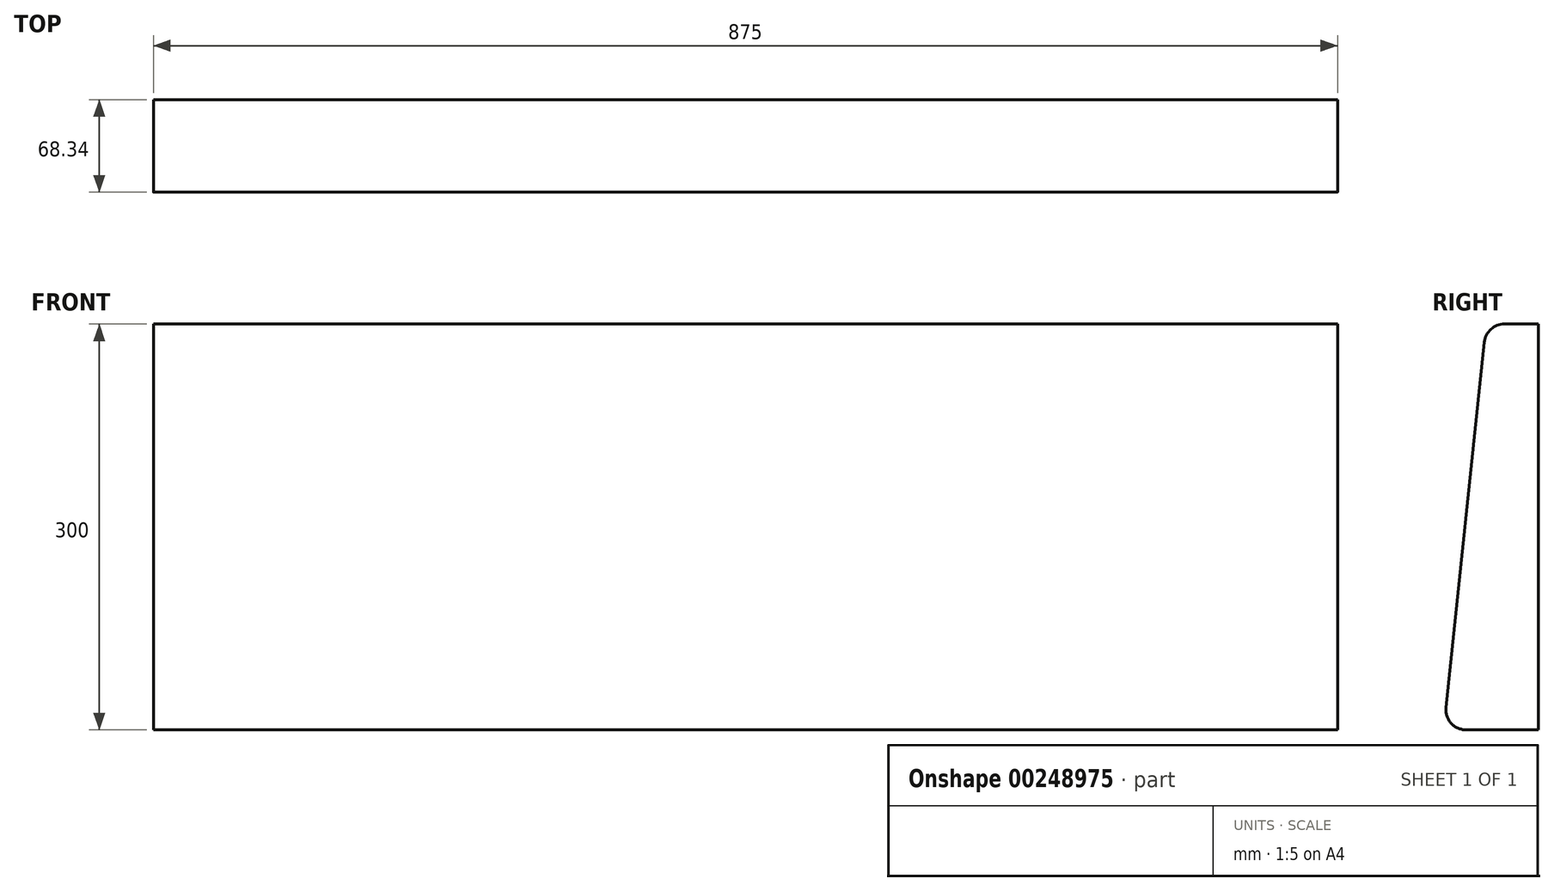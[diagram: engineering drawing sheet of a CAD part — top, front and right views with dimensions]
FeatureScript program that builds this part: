
annotation { "Feature Type Name" : "Feature", "Feature Type Description" : "" }
export const myFeature = defineFeature(function(context is Context, id is Id, definition is map)
    precondition{}
    {
        {
            var Q0;
            Q0=qCreatedBy(makeId("Right.planeOp"),FACE);
            var sketch = newSketch(context, id + "F0", { "sketchPlane" : qUnion([Q0])});
            skLineSegment(sketch, "E0.bottom", {"start": v(10.04, 150) * mm, "end": v(35, 150) * mm});
            skLineSegment(sketch, "E0.top", {"start": v(-18.34, -150) * mm, "end": v(35, -150) * mm});
            skLineSegment(sketch, "E0.right", {"start": v(35, 150) * mm, "end": v(35, -150) * mm});
            skPoint(sketch, "E0.middle", {"position": v(0, 0) * mm});
            skLineSegment(sketch, "E1", {"start": v(-33.26, -133.43) * mm, "end": v(-4.88, 136.57) * mm});
            skPoint(sketch, "E2.visualSharp", {"position": v(-3.47, 150) * mm});
            skArc(sketch, "E2.filletArc", {"start": v(10.04, 150) * mm, "mid": v(0, 146.15) * mm, "end": v(-4.88, 136.57) * mm});
            skPoint(sketch, "E3.visualSharp", {"position": v(-35, -150) * mm});
            skArc(sketch, "E3.filletArc", {"start": v(-33.26, -133.43) * mm, "mid": v(-29.49, -145.04) * mm, "end": v(-18.34, -150) * mm});
            skSolve(sketch);
        }
        {
            var Q0;
            Q0 = qSketchRegion(id + "F0", true);
            extrude(context, id + "F1", {"entities" : qUnion([Q0]), "depth" : 875 * mm});
        }
    });
